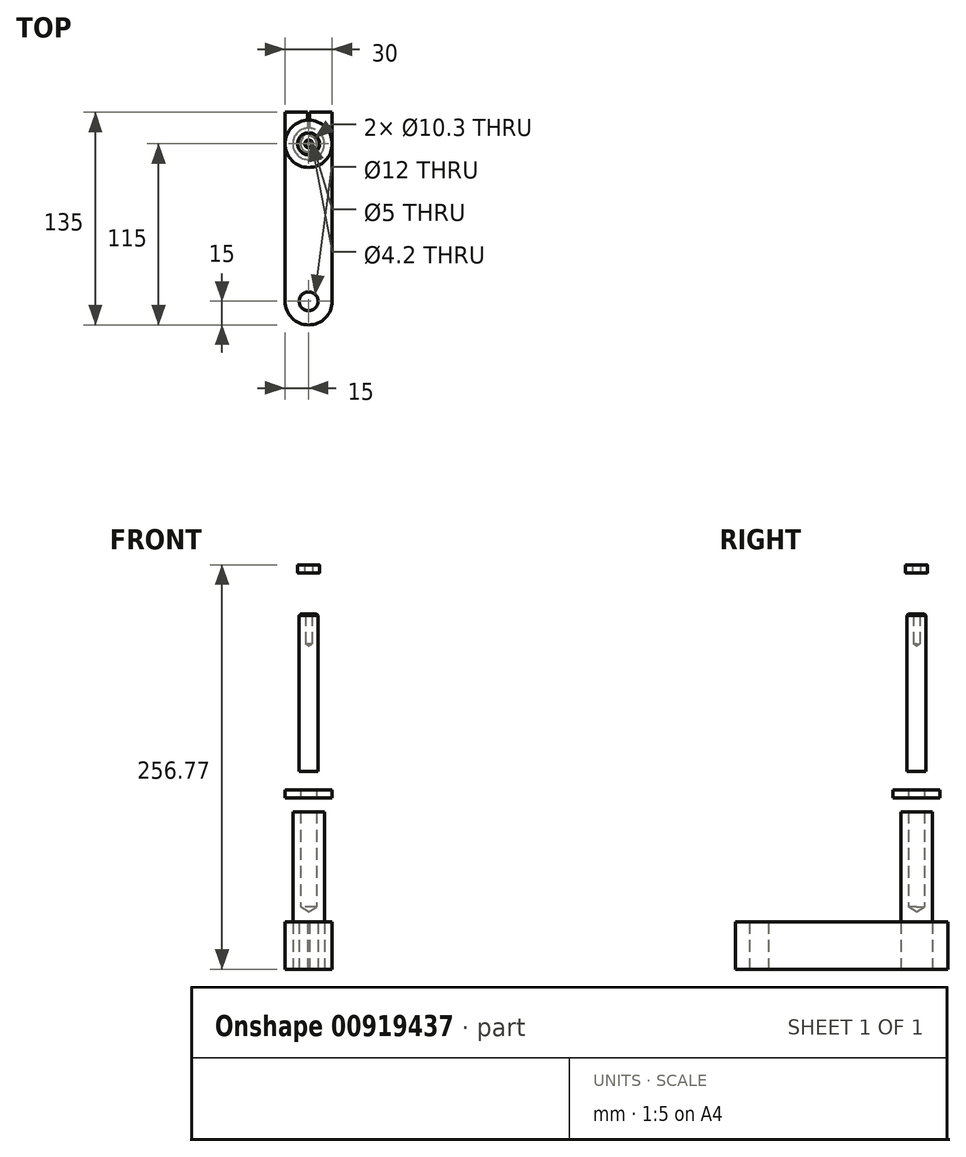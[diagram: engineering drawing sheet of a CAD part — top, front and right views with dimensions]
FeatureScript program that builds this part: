
annotation { "Feature Type Name" : "Feature", "Feature Type Description" : "" }
export const myFeature = defineFeature(function(context is Context, id is Id, definition is map)
    precondition{}
    {
        {
            var Q0;
            Q0=qCreatedBy(makeId("Front.planeOp"),FACE);
            var sketch = newSketch(context, id + "F0", { "sketchPlane" : qUnion([Q0])});
            skLineSegment(sketch, "E0", {"start": v(0, 0) * mm, "end": v(0, 271.24) * mm, "construction": true});
            skLineSegment(sketch, "E1.top", {"start": v(0, 0) * mm, "end": v(10, 0) * mm});
            skLineSegment(sketch, "E1.left", {"start": v(0, 100) * mm, "end": v(0, 0) * mm});
            skLineSegment(sketch, "E1.right", {"start": v(10, 100) * mm, "end": v(10, 0) * mm});
            skLineSegment(sketch, "E2.bottom", {"start": v(0, 125.61) * mm, "end": v(6, 125.61) * mm});
            skLineSegment(sketch, "E2.top", {"start": v(0, 225.61) * mm, "end": v(6, 225.61) * mm});
            skLineSegment(sketch, "E2.left", {"start": v(0, 125.61) * mm, "end": v(0, 225.61) * mm});
            skLineSegment(sketch, "E2.right", {"start": v(6, 125.61) * mm, "end": v(6, 225.61) * mm});
            skLineSegment(sketch, "E3", {"start": v(0, 100) * mm, "end": v(10, 100) * mm});
            skLineSegment(sketch, "E4.bottom", {"start": v(5.15, 113.74) * mm, "end": v(15, 113.74) * mm});
            skLineSegment(sketch, "E4.top", {"start": v(5.15, 108.74) * mm, "end": v(15, 108.74) * mm});
            skLineSegment(sketch, "E4.left", {"start": v(5.15, 113.74) * mm, "end": v(5.15, 108.74) * mm});
            skLineSegment(sketch, "E4.right", {"start": v(15, 113.74) * mm, "end": v(15, 108.74) * mm});
            skLineSegment(sketch, "E5.bottom", {"start": v(2.5, 256.77) * mm, "end": v(7, 256.77) * mm});
            skLineSegment(sketch, "E5.top", {"start": v(2.5, 251.77) * mm, "end": v(7, 251.77) * mm});
            skLineSegment(sketch, "E5.left", {"start": v(2.5, 256.77) * mm, "end": v(2.5, 251.77) * mm});
            skLineSegment(sketch, "E5.right", {"start": v(7, 256.77) * mm, "end": v(7, 251.77) * mm});
            skSolve(sketch);
        }
        {
            var Q0;
            Q0 = qSketchRegion(id + "F0", true);
            var Q1;
            Q1=sQuery(id+"F0.wireOp",EDGE,"E0");
            revolve(context, id + "F1", {"surfaceOperationType" : NewSurfaceOperationType.NEW, "entities" : qUnion([Q0]), "axis" : qUnion([Q1]), "revolveType" : RevolveType.FULL});
        }
        {
            var Q0;
            Q0=makeQuery(id+"F1.opRevolve","SWEPT_FACE",FACE,{"disambiguationData":[OSD([sQuery(id+"F0.wireOp",EDGE,"E3")])]});
            var sketch = newSketch(context, id + "F2", { "sketchPlane" : qUnion([Q0])});
            skPoint(sketch, "E6", {"position": v(0, 0) * mm});
            skSolve(sketch);
        }
        {
            var Q0;
            Q0=sQuery(id+"F2.wireOp",VERTEX,"E6");
            var Q1;
            Q1=makeQuery(id+"F1.opRevolve","SWEPT_BODY",BODY,{"disambiguationData":[OSD([sQuery(id+"F0.wireOp",EDGE,"E1.top"),sQuery(id+"F0.wireOp",EDGE,"E1.left"),sQuery(id+"F0.wireOp",EDGE,"E1.right"),sQuery(id+"F0.wireOp",EDGE,"E3")])]});
            hole(context, id + "F3", {"style" : HoleStyle.SIMPLE, "endStyle" : HoleEndStyle.BLIND, "standardTappedOrClearance" : lookupTablePath({ "standard" : "ISO", "engagement" : "75%", "pitch" : "1.75 mm", "size" : "M12", "type" : "Tapped" }), "standardBlindInLast" : lookupTablePath({ "standard" : "ISO", "engagement" : "75%", "pitch" : "1.75 mm", "size" : "M12", "type" : "Tapped" }), "holeDiameter" : 10.3 * mm, "majorDiameter" : 12 * mm, "showTappedDepth" : true, "holeDepth" : 60.5 * mm, "tappedDepth" : 50 * mm, "tapClearance" : 6, "locations" : qUnion([Q0]), "scope" : qUnion([Q1]), "startStyle" : HoleStartStyle.SKETCH});
        }
        {
            var Q0;
            Q0=makeQuery(id+"F1.opRevolve","SWEPT_FACE",FACE,{"disambiguationData":[OSD([sQuery(id+"F0.wireOp",EDGE,"E5.left")])]});
            var Q1;
            Q1=makeQuery(id+"F1.opRevolve","SWEPT_FACE",FACE,{"disambiguationData":[OSD([sQuery(id+"F0.wireOp",EDGE,"E5.right")])]});
            fillet(context, id + "F4", {"entities" : qUnion([Q0, Q1]), "radius" : 0.2 * mm, "tangentPropagation" : true, "allowEdgeOverflow" : false});
        }
        {
            var Q0;
            Q0=makeQuery(id+"F1.opRevolve","SWEPT_FACE",FACE,{"disambiguationData":[OSD([sQuery(id+"F0.wireOp",EDGE,"E2.top")])]});
            var sketch = newSketch(context, id + "F5", { "sketchPlane" : qUnion([Q0])});
            skPoint(sketch, "E7", {"position": v(0, 0) * mm});
            skSolve(sketch);
        }
        {
            var Q0;
            Q0=sQuery(id+"F5.wireOp",VERTEX,"E7");
            var Q1;
            Q1=makeQuery(id+"F1.opRevolve","SWEPT_BODY",BODY,{"disambiguationData":[OSD([sQuery(id+"F0.wireOp",EDGE,"E2.bottom"),sQuery(id+"F0.wireOp",EDGE,"E2.top"),sQuery(id+"F0.wireOp",EDGE,"E2.left"),sQuery(id+"F0.wireOp",EDGE,"E2.right")])]});
            hole(context, id + "F6", {"style" : HoleStyle.SIMPLE, "endStyle" : HoleEndStyle.BLIND, "standardTappedOrClearance" : lookupTablePath({ "standard" : "ISO", "engagement" : "75%", "pitch" : "0.8 mm", "size" : "M5", "type" : "Tapped" }), "standardBlindInLast" : lookupTablePath({ "standard" : "ISO", "engagement" : "75%", "pitch" : "0.8 mm", "size" : "M5", "type" : "Tapped" }), "holeDiameter" : 4.2 * mm, "majorDiameter" : 5 * mm, "showTappedDepth" : true, "holeDepth" : 19 * mm, "tappedDepth" : 15 * mm, "tapClearance" : 5, "locations" : qUnion([Q0]), "scope" : qUnion([Q1]), "startStyle" : HoleStartStyle.SKETCH});
        }
        {
            var Q0;
            Q0=makeQuery(id+"F1.opRevolve","SWEPT_EDGE",EDGE,{"disambiguationData":[OSD([sQuery(id+"F0.wireOp",EDGE,"E2.top"),sQuery(id+"F0.wireOp",EDGE,"E2.right")])]});
            chamfer(context, id + "F7", {"entities" : qUnion([Q0]), "width" : 1 * mm, "tangentPropagation" : true});
        }
        {
            var Q0;
            Q0=qCreatedBy(makeId("Top.planeOp"),FACE);
            var sketch = newSketch(context, id + "F8", { "sketchPlane" : qUnion([Q0])});
            skLineSegment(sketch, "E8", {"start": v(-15, 20) * mm, "end": v(-15, -100) * mm});
            skLineSegment(sketch, "E9", {"start": v(15, 20) * mm, "end": v(15, -100) * mm});
            skArc(sketch, "E10", {"start": v(-15, -100) * mm, "mid": v(0, -115) * mm, "end": v(15, -100) * mm});
            skLineSegment(sketch, "E11", {"start": v(-15, 20) * mm, "end": v(-0.75, 20) * mm});
            skLineSegment(sketch, "E12", {"start": v(-0.75, 20) * mm, "end": v(-0.75, 9.97) * mm});
            skLineSegment(sketch, "E13", {"start": v(15, 20) * mm, "end": v(0.75, 20) * mm});
            skLineSegment(sketch, "E14", {"start": v(0.75, 20) * mm, "end": v(0.75, 9.97) * mm});
            skArc(sketch, "E15", {"start": v(-0.75, 9.97) * mm, "mid": v(0, -10) * mm, "end": v(0.75, 9.97) * mm});
            skCircle(sketch, "E16", {"center": v(0, -100) * mm, "radius": 6 * mm});
            skSolve(sketch);
        }
        {
            var Q0;
            Q0 = qSketchRegion(id + "F8", true);
            extrude(context, id + "F9", {"entities" : qUnion([Q0]), "depth" : 30 * mm, "offsetDistance" : 25 * mm});
        }
    });
